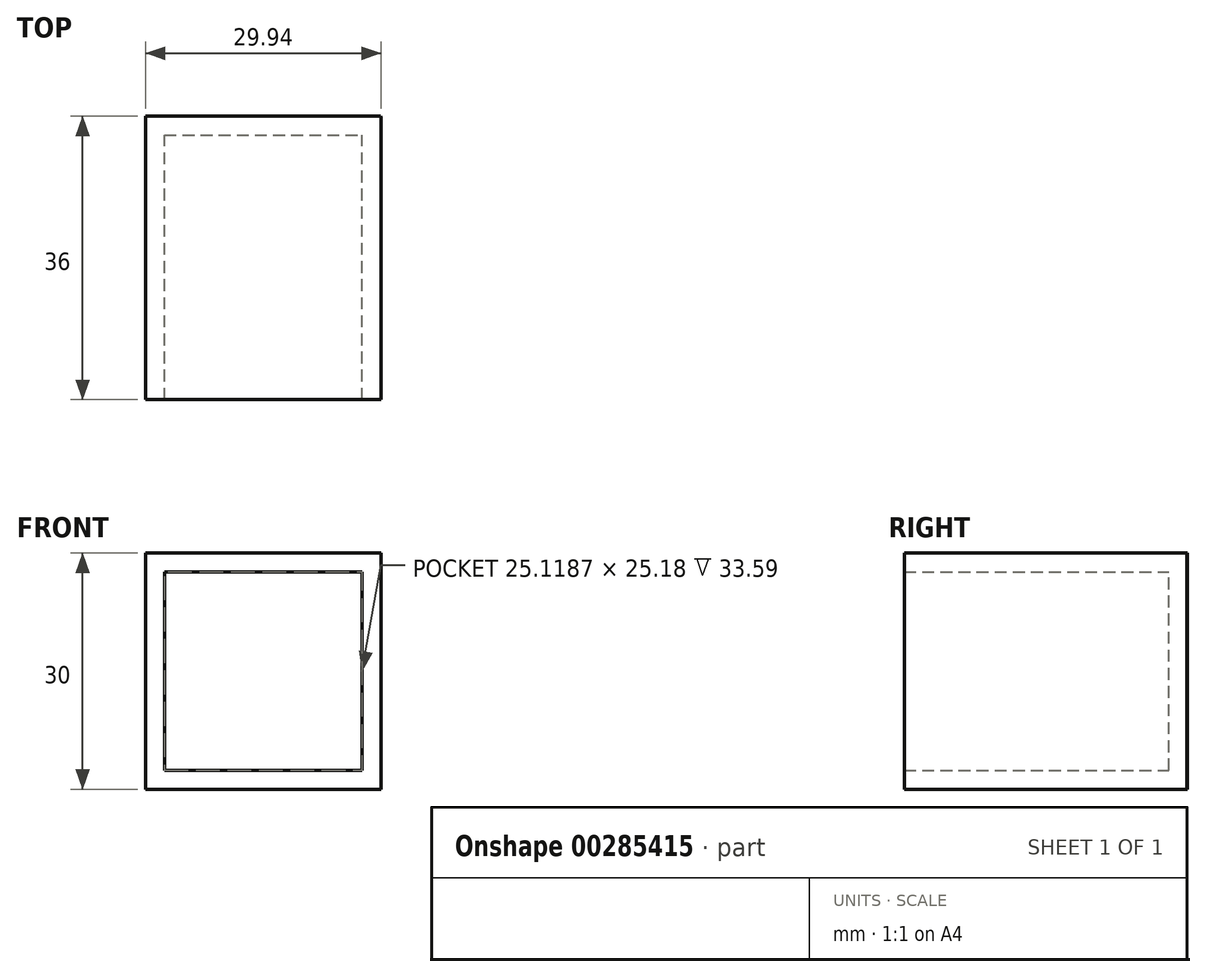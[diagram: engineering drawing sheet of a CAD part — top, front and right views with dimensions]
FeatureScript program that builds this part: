
annotation { "Feature Type Name" : "Feature", "Feature Type Description" : "" }
export const myFeature = defineFeature(function(context is Context, id is Id, definition is map)
    precondition{}
    {
        {
            var Q0;
            Q0=qCreatedBy(makeId("Front.planeOp"),FACE);
            var sketch = newSketch(context, id + "F0", { "sketchPlane" : qUnion([Q0])});
            skLineSegment(sketch, "E0.bottom", {"start": v(0, 0) * mm, "end": v(29.94, 0) * mm});
            skLineSegment(sketch, "E0.top", {"start": v(0, 30) * mm, "end": v(29.94, 30) * mm});
            skLineSegment(sketch, "E0.left", {"start": v(0, 0) * mm, "end": v(0, 30) * mm});
            skLineSegment(sketch, "E0.right", {"start": v(29.94, 0) * mm, "end": v(29.94, 30) * mm});
            skSolve(sketch);
        }
        {
            var Q0;
            Q0=makeQuery(id+"F0.imprint","IMPRINT",FACE,{"disambiguationData":[TD([[makeQuery(id+"F0.imprint","IMPRINT",EDGE,{"derivedFrom":sQuery(id+"F0.wireOp",EDGE,"E0.bottom")}),1.0]])]});
            extrude(context, id + "F1", {"entities" : qUnion([Q0]), "depth" : 36 * mm});
        }
        {
            var Q0;
            Q0=makeQuery(id+"F1.opExtrude","CAP_FACE",FACE,{"disambiguationData":[OSD([sQuery(id+"F0.wireOp",EDGE,"E0.bottom"),sQuery(id+"F0.wireOp",EDGE,"E0.top"),sQuery(id+"F0.wireOp",EDGE,"E0.left"),sQuery(id+"F0.wireOp",EDGE,"E0.right")])],"isStart":false});
            shell(context, id + "F2", {"entities" : qUnion([Q0]), "thickness" : 2.41 * mm});
        }
        {
            var Q0;
            Q0=makeQuery(id+"F1.opExtrude","CAP_EDGE",EDGE,{"disambiguationData":[OSD([sQuery(id+"F0.wireOp",EDGE,"E0.right")])],"isStart":true});
            chamfer(context, id + "F3", {"entities" : qUnion([Q0]), "width" : 0.1 * mm, "tangentPropagation" : true});
        }
    });
